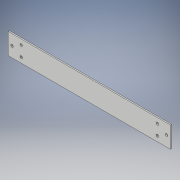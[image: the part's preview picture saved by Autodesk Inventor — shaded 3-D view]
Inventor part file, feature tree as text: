
AUTODESK INVENTOR PART (.ipt)
format: ipt  version: 2017 (Build 210142000, 142)  size: 107,520 bytes
history: native  units: in
note: dims shown in document units (in); Inventor stores cm internally (conversion verified against a paired STEP export)
features: extrude x1
ambient origin geometry x8: Origin, YZ Plane, XZ Plane, XY Plane, X Axis, Y Axis, Z Axis, Center Point
bodies: Body1 (feature_tree)
feature tree (1):
  extrude  "Extrusion2"  Depth=15.5in
